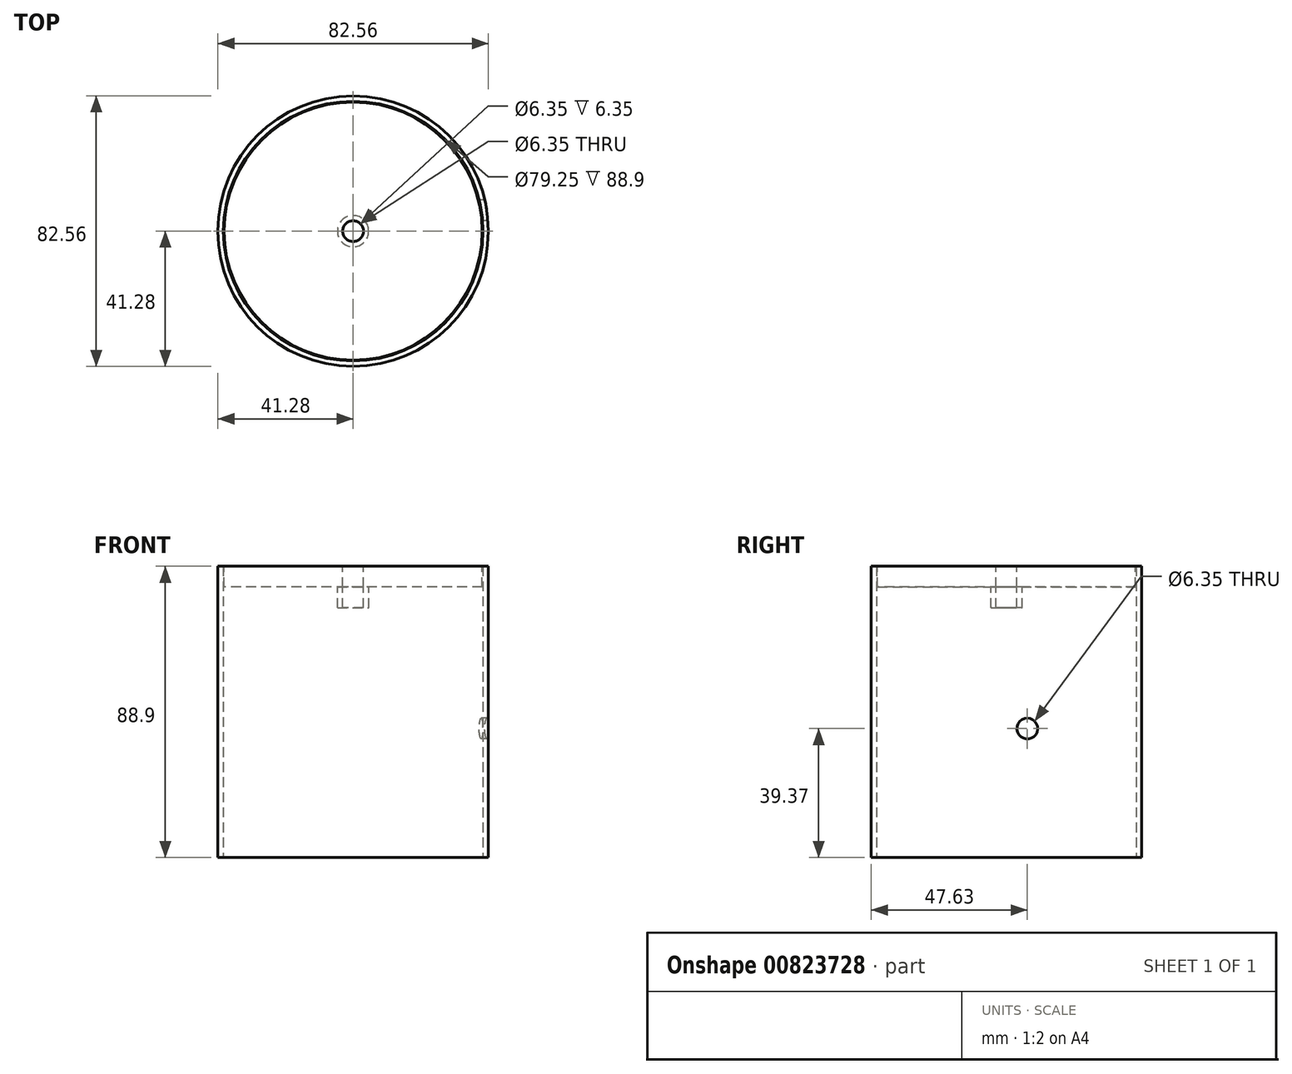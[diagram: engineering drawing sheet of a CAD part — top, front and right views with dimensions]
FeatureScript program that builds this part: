
annotation { "Feature Type Name" : "Feature", "Feature Type Description" : "" }
export const myFeature = defineFeature(function(context is Context, id is Id, definition is map)
    precondition{}
    {
        {
            var Q0;
            Q0=qCreatedBy(makeId("Top.planeOp"),FACE);
            var sketch = newSketch(context, id + "F0", { "sketchPlane" : qUnion([Q0])});
            skCircle(sketch, "E0", {"center": v(0, 0) * mm, "radius": 39.62 * mm});
            skCircle(sketch, "E1", {"center": v(0, 0) * mm, "radius": 41.28 * mm});
            skSolve(sketch);
        }
        {
            var Q0;
            Q0=qSketchRegion(id+"F0",true);
            extrude(context, id + "F1", {"entities" : qUnion([Q0]), "depth" : 88.9 * mm, "offsetDistance" : 25.4 * mm});
        }
        {
            var Q0;
            Q0=makeQuery(id+"F1.opExtrude","CAP_FACE",FACE,{"disambiguationData":[OSD([sQuery(id+"F0.wireOp",EDGE,"E0"),sQuery(id+"F0.wireOp",EDGE,"E1")])],"isStart":false});
            var sketch = newSketch(context, id + "F2", { "sketchPlane" : qUnion([Q0])});
            skCircle(sketch, "E2", {"center": v(0, 0) * mm, "radius": 39.37 * mm});
            skCircle(sketch, "E3", {"center": v(0, 0) * mm, "radius": 3.18 * mm});
            skSolve(sketch);
        }
        {
            var Q0;
            Q0=qSketchRegion(id+"F2",true);
            extrude(context, id + "F3", {"entities" : qUnion([Q0]), "oppositeDirection" : true, "depth" : 6.35 * mm, "offsetDistance" : 25.4 * mm});
        }
        {
            var Q0;
            Q0=qCreatedBy(makeId("Right.planeOp"),FACE);
            var sketch = newSketch(context, id + "F4", { "sketchPlane" : qUnion([Q0])});
            skCircle(sketch, "E4", {"center": v(6.35, 39.37) * mm, "radius": 3.18 * mm});
            skSolve(sketch);
        }
        {
            var Q0;
            Q0=qSketchRegion(id+"F4",true);
            extrude(context, id + "F5", {"entities" : qUnion([Q0]), "operationType" : NewBodyOperationType.REMOVE, "depth" : 127 * mm, "offsetDistance" : 25.4 * mm});
        }
        {
            var Q0;
            Q0=makeQuery(id+"F3.opExtrude","CAP_FACE",FACE,{"disambiguationData":[OSD([sQuery(id+"F2.wireOp",EDGE,"E2"),sQuery(id+"F2.wireOp",EDGE,"E3")])],"isStart":false});
            var sketch = newSketch(context, id + "F6", { "sketchPlane" : qUnion([Q0])});
            skCircle(sketch, "E5", {"center": v(0, 0) * mm, "radius": 4.76 * mm});
            skCircle(sketch, "E6", {"center": v(0, 0) * mm, "radius": 3.18 * mm});
            skSolve(sketch);
        }
        {
            var Q0;
            Q0=qSketchRegion(id+"F6",true);
            extrude(context, id + "F7", {"entities" : qUnion([Q0]), "depth" : 6.35 * mm, "offsetDistance" : 25.4 * mm});
        }
    });
